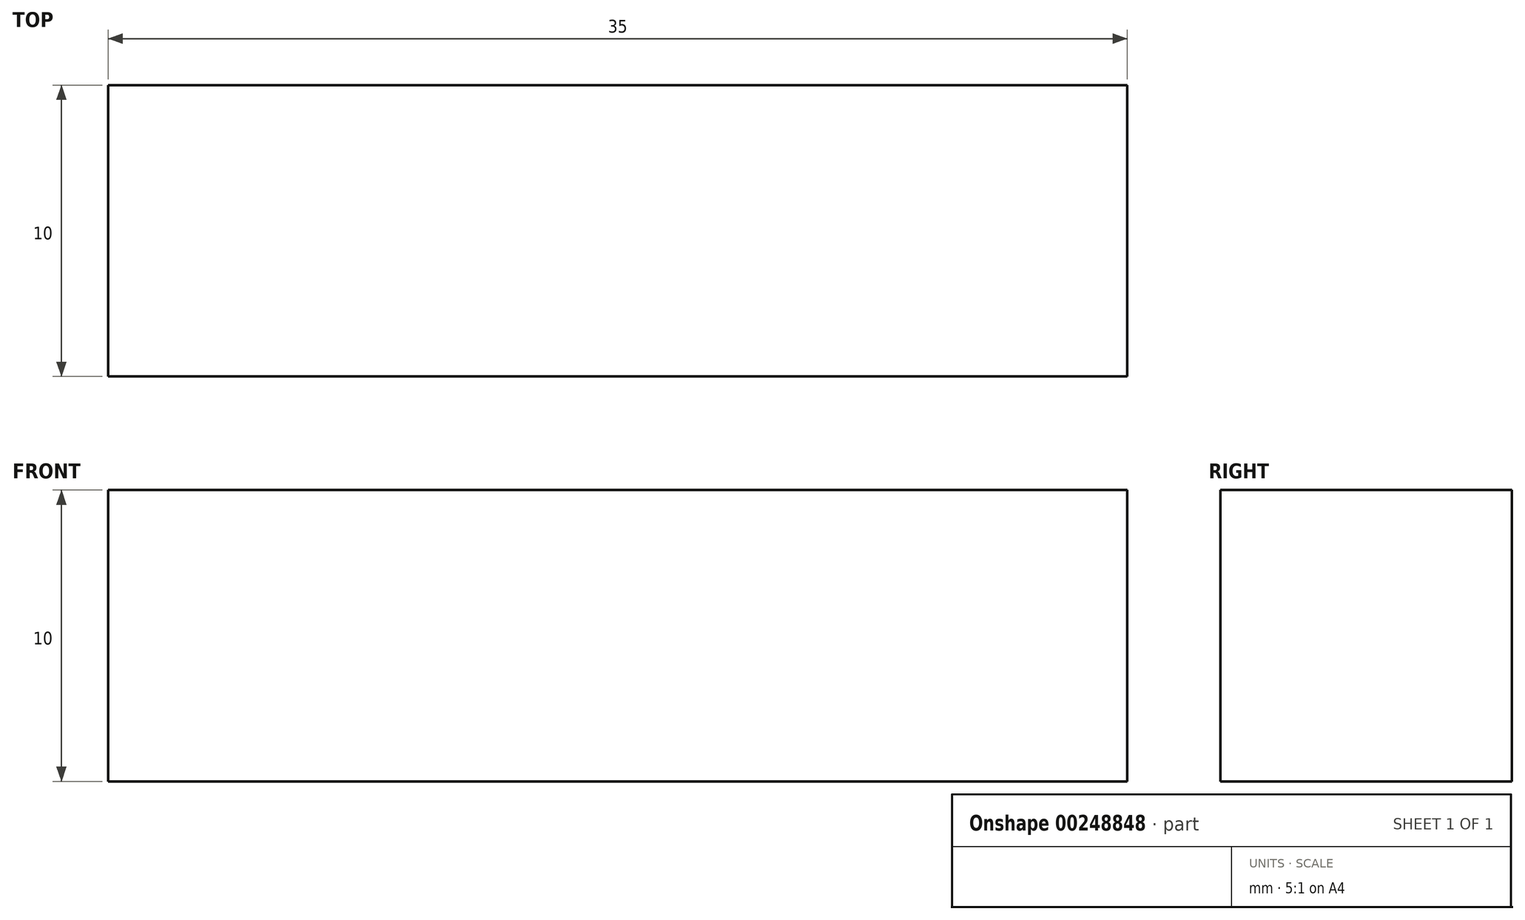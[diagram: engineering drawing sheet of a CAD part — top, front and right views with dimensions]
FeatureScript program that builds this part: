
annotation { "Feature Type Name" : "Feature", "Feature Type Description" : "" }
export const myFeature = defineFeature(function(context is Context, id is Id, definition is map)
    precondition{}
    {
        {
            var Q0;
            Q0=qCreatedBy(makeId("Front.planeOp"),FACE);
            var sketch = newSketch(context, id + "F0", { "sketchPlane" : qUnion([Q0])});
            skLineSegment(sketch, "E0.bottom", {"start": v(-5, -200) * mm, "end": v(5, -200) * mm});
            skLineSegment(sketch, "E0.top", {"start": v(-5, 200) * mm, "end": v(5, 200) * mm});
            skLineSegment(sketch, "E0.left", {"start": v(-5, -200) * mm, "end": v(-5, 200) * mm});
            skLineSegment(sketch, "E0.right", {"start": v(5, -200) * mm, "end": v(5, 200) * mm});
            skPoint(sketch, "E0.middle", {"position": v(0, 0) * mm});
            skLineSegment(sketch, "E1.bottom", {"start": v(-50, 195) * mm, "end": v(50, 195) * mm});
            skLineSegment(sketch, "E1.top", {"start": v(-50, 205) * mm, "end": v(50, 205) * mm});
            skLineSegment(sketch, "E1.left", {"start": v(-50, 195) * mm, "end": v(-50, 205) * mm});
            skLineSegment(sketch, "E1.right", {"start": v(50, 195) * mm, "end": v(50, 205) * mm});
            skPoint(sketch, "E1.middle", {"position": v(0, 200) * mm});
            skLineSegment(sketch, "E2", {"start": v(-5, -200) * mm, "end": v(-5, -141.64) * mm});
            skLineSegment(sketch, "E3", {"start": v(0, -200) * mm, "end": v(0, -140) * mm});
            skPoint(sketch, "E3.endSnap0", {"position": v(0, -200) * mm});
            skLineSegment(sketch, "E4", {"start": v(-25, -140) * mm, "end": v(0, -140) * mm});
            skLineSegment(sketch, "E5", {"start": v(-25, -140) * mm, "end": v(-25, -130) * mm});
            skLineSegment(sketch, "E6", {"start": v(-25, -130) * mm, "end": v(0, -130) * mm});
            skLineSegment(sketch, "E7", {"start": v(0, -130) * mm, "end": v(0, -140) * mm});
            skLineSegment(sketch, "E8", {"start": v(-25, -130) * mm, "end": v(-35, -130) * mm});
            skLineSegment(sketch, "E9", {"start": v(-25, -140) * mm, "end": v(-35, -140) * mm});
            skLineSegment(sketch, "E10", {"start": v(-35, -140) * mm, "end": v(-35, -130) * mm});
            skSolve(sketch);
        }
        {
            var Q0;
            Q0=makeQuery(id+"F0.imprint","IMPRINT",FACE,{"disambiguationData":[TD([[makeQuery(id+"F0.imprint","IMPRINT",EDGE,{"derivedFrom":sQuery(id+"F0.wireOp",EDGE,"E5")}),1.0]])]});
            var Q1;
            {var subQ5=sQuery(id+"F0.wireOp",EDGE,"E5");Q1=makeQuery(id+"F0.imprint","IMPRINT",FACE,{"disambiguationData":[TD([[makeQuery(id+"F0.imprint","IMPRINT",EDGE,{"derivedFrom":subQ5}),-1.0]])]});}
            var Q2;
            {var subQ5=sQuery(id+"F0.wireOp",EDGE,"E7");Q2=makeQuery(id+"F0.imprint","IMPRINT",FACE,{"disambiguationData":[TD([[makeQuery(id+"F0.imprint","IMPRINT",EDGE,{"derivedFrom":subQ5}),-1.0]])]});}
            extrude(context, id + "F1", {"entities" : qUnion([Q0, Q1, Q2]), "endBound" : BoundingType.SYMMETRIC, "depth" : 10 * mm});
        }
    });
